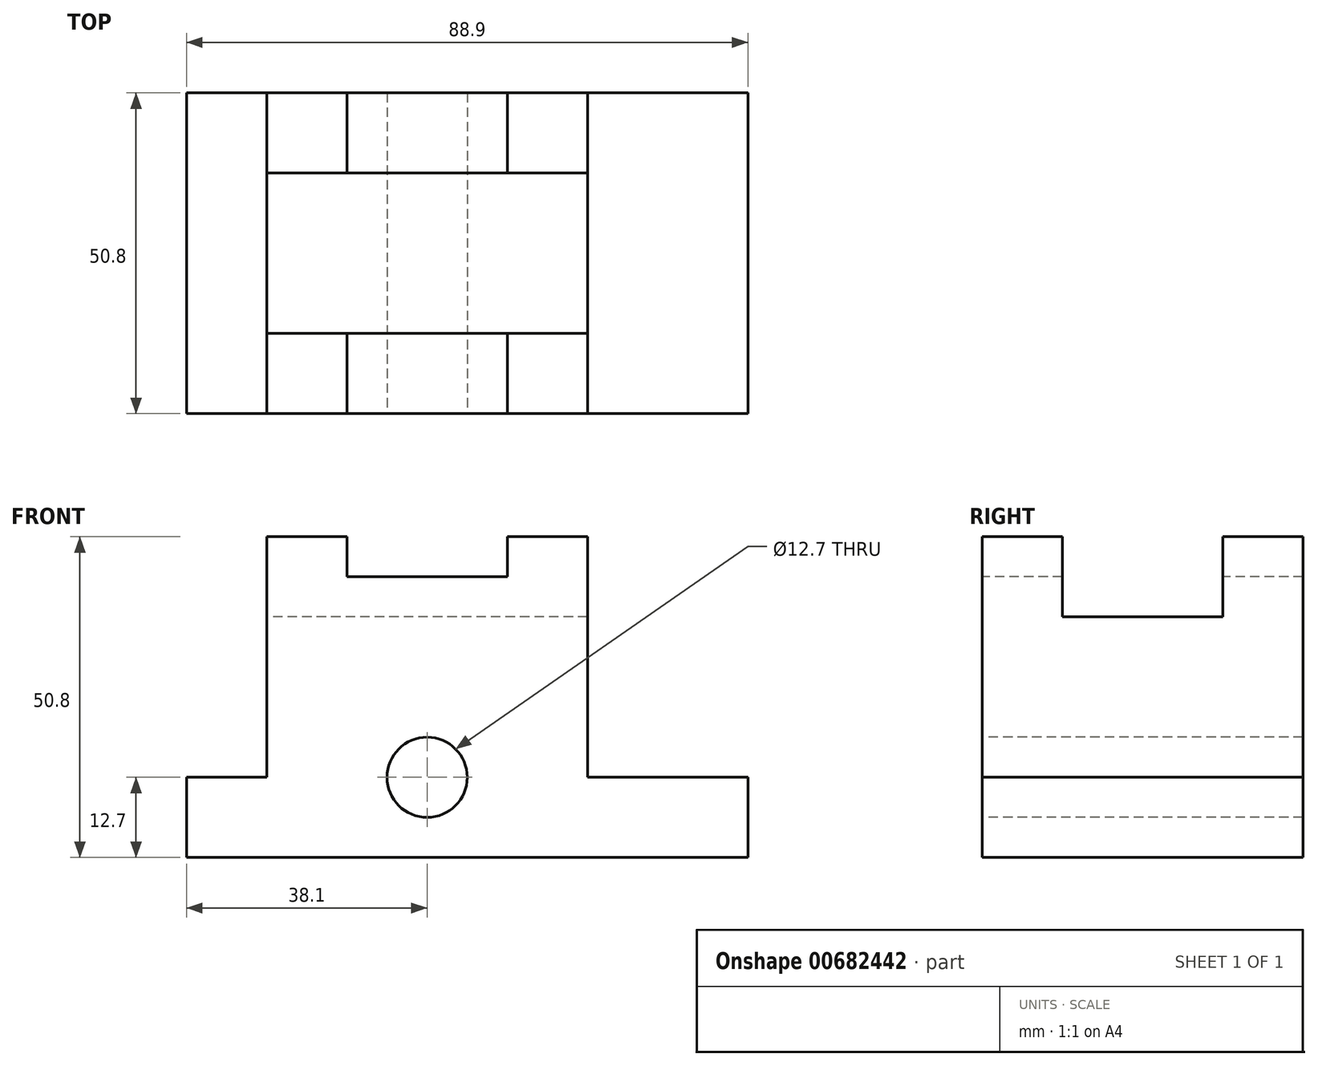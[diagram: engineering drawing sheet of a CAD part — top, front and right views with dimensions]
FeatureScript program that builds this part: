
annotation { "Feature Type Name" : "Feature", "Feature Type Description" : "" }
export const myFeature = defineFeature(function(context is Context, id is Id, definition is map)
    precondition{}
    {
        {
            var Q0;
            Q0=qCreatedBy(makeId("Front.planeOp"),FACE);
            var sketch = newSketch(context, id + "F0", { "sketchPlane" : qUnion([Q0])});
            skLineSegment(sketch, "E0.bottom", {"start": v(-44.45, 19.05) * mm, "end": v(44.45, 19.05) * mm});
            skLineSegment(sketch, "E0.top", {"start": v(-44.45, -19.05) * mm, "end": v(44.45, -19.05) * mm});
            skLineSegment(sketch, "E0.left", {"start": v(-44.45, 19.05) * mm, "end": v(-44.45, -19.05) * mm});
            skLineSegment(sketch, "E0.right", {"start": v(44.45, 19.05) * mm, "end": v(44.45, -19.05) * mm});
            skPoint(sketch, "E0.middle", {"position": v(0, 0) * mm});
            skSolve(sketch);
        }
        {
            var Q0;
            Q0=makeQuery(id+"F0.imprint","IMPRINT",FACE,{"disambiguationData":[TD([[makeQuery(id+"F0.imprint","IMPRINT",EDGE,{"derivedFrom":sQuery(id+"F0.wireOp",EDGE,"E0.bottom")}),-1.0]])]});
            extrude(context, id + "F1", {"entities" : qUnion([Q0]), "depth" : 50.8 * mm, "offsetDistance" : 25.4 * mm});
        }
        {
            var Q0;
            Q0=makeQuery(id+"F1.opExtrude","CAP_FACE",FACE,{"disambiguationData":[OSD([sQuery(id+"F0.wireOp",EDGE,"E0.bottom"),sQuery(id+"F0.wireOp",EDGE,"E0.top"),sQuery(id+"F0.wireOp",EDGE,"E0.left"),sQuery(id+"F0.wireOp",EDGE,"E0.right")])],"isStart":false});
            var sketch = newSketch(context, id + "F2", { "sketchPlane" : qUnion([Q0])});
            skLineSegment(sketch, "E1.bottom", {"start": v(-44.45, 19.05) * mm, "end": v(-31.75, 19.05) * mm});
            skLineSegment(sketch, "E1.top", {"start": v(-44.45, -6.35) * mm, "end": v(-31.75, -6.35) * mm});
            skLineSegment(sketch, "E1.left", {"start": v(-44.45, 19.05) * mm, "end": v(-44.45, -6.35) * mm});
            skLineSegment(sketch, "E1.right", {"start": v(-31.75, 19.05) * mm, "end": v(-31.75, -6.35) * mm});
            skSolve(sketch);
        }
        {
            var Q0;
            Q0=makeQuery(id+"F2.imprint","IMPRINT",FACE,{"disambiguationData":[TD([[makeQuery(id+"F2.imprint","IMPRINT",EDGE,{"derivedFrom":sQuery(id+"F2.wireOp",EDGE,"E1.bottom")}),-1.0]])]});
            extrude(context, id + "F3", {"entities" : qUnion([Q0]), "operationType" : NewBodyOperationType.REMOVE, "endBound" : BoundingType.THROUGH_ALL, "oppositeDirection" : true, "depth" : 25.4 * mm, "offsetDistance" : 25.4 * mm});
        }
        {
            var Q0;
            Q0=makeQuery(id+"F1.opExtrude","CAP_FACE",FACE,{"disambiguationData":[OSD([sQuery(id+"F0.wireOp",EDGE,"E0.bottom"),sQuery(id+"F0.wireOp",EDGE,"E0.top"),sQuery(id+"F0.wireOp",EDGE,"E0.left"),sQuery(id+"F0.wireOp",EDGE,"E0.right")])],"isStart":false});
            var sketch = newSketch(context, id + "F4", { "sketchPlane" : qUnion([Q0])});
            skLineSegment(sketch, "E2.bottom", {"start": v(44.45, 19.05) * mm, "end": v(19.05, 19.05) * mm});
            skLineSegment(sketch, "E2.top", {"start": v(44.45, -6.35) * mm, "end": v(19.05, -6.35) * mm});
            skLineSegment(sketch, "E2.left", {"start": v(44.45, 19.05) * mm, "end": v(44.45, -6.35) * mm});
            skLineSegment(sketch, "E2.right", {"start": v(19.05, 19.05) * mm, "end": v(19.05, -6.35) * mm});
            skSolve(sketch);
        }
        {
            var Q0;
            Q0=makeQuery(id+"F4.imprint","IMPRINT",FACE,{"disambiguationData":[TD([[makeQuery(id+"F4.imprint","IMPRINT",EDGE,{"derivedFrom":sQuery(id+"F4.wireOp",EDGE,"E2.bottom")}),-1.0]])]});
            extrude(context, id + "F5", {"entities" : qUnion([Q0]), "operationType" : NewBodyOperationType.REMOVE, "endBound" : BoundingType.THROUGH_ALL, "oppositeDirection" : true, "depth" : 25.4 * mm, "offsetDistance" : 25.4 * mm});
        }
        {
            var Q0;
            Q0=makeQuery(id+"F1.opExtrude","SWEPT_FACE",FACE,{"disambiguationData":[OSD([sQuery(id+"F0.wireOp",EDGE,"E0.bottom")])]});
            var sketch = newSketch(context, id + "F6", { "sketchPlane" : qUnion([Q0])});
            skLineSegment(sketch, "E3.bottom", {"start": v(-31.75, 0) * mm, "end": v(19.05, 0) * mm});
            skLineSegment(sketch, "E3.top", {"start": v(-31.75, -12.7) * mm, "end": v(19.05, -12.7) * mm});
            skLineSegment(sketch, "E3.left", {"start": v(-31.75, 0) * mm, "end": v(-31.75, -12.7) * mm});
            skLineSegment(sketch, "E3.right", {"start": v(19.05, 0) * mm, "end": v(19.05, -12.7) * mm});
            skLineSegment(sketch, "E4.bottom", {"start": v(19.05, -50.8) * mm, "end": v(-31.75, -50.8) * mm});
            skLineSegment(sketch, "E4.top", {"start": v(19.05, -38.1) * mm, "end": v(-31.75, -38.1) * mm});
            skLineSegment(sketch, "E4.left", {"start": v(19.05, -50.8) * mm, "end": v(19.05, -38.1) * mm});
            skLineSegment(sketch, "E4.right", {"start": v(-31.75, -50.8) * mm, "end": v(-31.75, -38.1) * mm});
            skSolve(sketch);
        }
        {
            var Q0;
            Q0=makeQuery(id+"F6.imprint","IMPRINT",FACE,{"disambiguationData":[TD([[makeQuery(id+"F6.imprint","IMPRINT",EDGE,{"derivedFrom":sQuery(id+"F6.wireOp",EDGE,"E3.bottom")}),-1.0]])]});
            var Q1;
            Q1=makeQuery(id+"F6.imprint","IMPRINT",FACE,{"disambiguationData":[TD([[makeQuery(id+"F6.imprint","IMPRINT",EDGE,{"derivedFrom":sQuery(id+"F6.wireOp",EDGE,"E4.bottom")}),1.0]])]});
            extrude(context, id + "F7", {"entities" : qUnion([Q0, Q1]), "operationType" : NewBodyOperationType.ADD, "depth" : 6.35 * mm, "offsetDistance" : 25.4 * mm});
        }
        {
            var Q0;
            Q0=makeQuery(id+"F7.opExtrude","CAP_FACE",FACE,{"disambiguationData":[OSD([sQuery(id+"F6.wireOp",EDGE,"E3.bottom"),sQuery(id+"F6.wireOp",EDGE,"E3.top"),sQuery(id+"F6.wireOp",EDGE,"E3.left"),sQuery(id+"F6.wireOp",EDGE,"E3.right")])],"isStart":false});
            var sketch = newSketch(context, id + "F8", { "sketchPlane" : qUnion([Q0])});
            skLineSegment(sketch, "E5.bottom", {"start": v(-31.75, 0) * mm, "end": v(-19.05, 0) * mm});
            skLineSegment(sketch, "E5.top", {"start": v(-31.75, -12.7) * mm, "end": v(-19.05, -12.7) * mm});
            skLineSegment(sketch, "E5.left", {"start": v(-31.75, 0) * mm, "end": v(-31.75, -12.7) * mm});
            skLineSegment(sketch, "E5.right", {"start": v(-19.05, 0) * mm, "end": v(-19.05, -12.7) * mm});
            skLineSegment(sketch, "E6.bottom", {"start": v(19.05, 0) * mm, "end": v(6.35, 0) * mm});
            skLineSegment(sketch, "E6.top", {"start": v(19.05, -12.7) * mm, "end": v(6.35, -12.7) * mm});
            skLineSegment(sketch, "E6.left", {"start": v(19.05, 0) * mm, "end": v(19.05, -12.7) * mm});
            skLineSegment(sketch, "E6.right", {"start": v(6.35, 0) * mm, "end": v(6.35, -12.7) * mm});
            skSolve(sketch);
        }
        {
            var Q0;
            Q0=makeQuery(id+"F8.imprint","IMPRINT",FACE,{"disambiguationData":[TD([[makeQuery(id+"F8.imprint","IMPRINT",EDGE,{"derivedFrom":sQuery(id+"F8.wireOp",EDGE,"E5.bottom")}),-1.0]])]});
            var Q1;
            Q1=makeQuery(id+"F8.imprint","IMPRINT",FACE,{"disambiguationData":[TD([[makeQuery(id+"F8.imprint","IMPRINT",EDGE,{"derivedFrom":sQuery(id+"F8.wireOp",EDGE,"E6.bottom")}),-1.0]])]});
            extrude(context, id + "F9", {"entities" : qUnion([Q0, Q1]), "operationType" : NewBodyOperationType.ADD, "depth" : 6.35 * mm, "offsetDistance" : 25.4 * mm});
        }
        {
            var Q0;
            Q0=makeQuery(id+"F7.opExtrude","CAP_FACE",FACE,{"disambiguationData":[OSD([sQuery(id+"F6.wireOp",EDGE,"E4.bottom"),sQuery(id+"F6.wireOp",EDGE,"E4.top"),sQuery(id+"F6.wireOp",EDGE,"E4.left"),sQuery(id+"F6.wireOp",EDGE,"E4.right")])],"isStart":false});
            var sketch = newSketch(context, id + "F10", { "sketchPlane" : qUnion([Q0])});
            skLineSegment(sketch, "E7.bottom", {"start": v(-31.75, -38.1) * mm, "end": v(-19.05, -38.1) * mm});
            skLineSegment(sketch, "E7.top", {"start": v(-31.75, -50.8) * mm, "end": v(-19.05, -50.8) * mm});
            skLineSegment(sketch, "E7.left", {"start": v(-31.75, -38.1) * mm, "end": v(-31.75, -50.8) * mm});
            skLineSegment(sketch, "E7.right", {"start": v(-19.05, -38.1) * mm, "end": v(-19.05, -50.8) * mm});
            skLineSegment(sketch, "E8.bottom", {"start": v(19.05, -38.1) * mm, "end": v(6.35, -38.1) * mm});
            skLineSegment(sketch, "E8.top", {"start": v(19.05, -50.8) * mm, "end": v(6.35, -50.8) * mm});
            skLineSegment(sketch, "E8.left", {"start": v(19.05, -38.1) * mm, "end": v(19.05, -50.8) * mm});
            skLineSegment(sketch, "E8.right", {"start": v(6.35, -38.1) * mm, "end": v(6.35, -50.8) * mm});
            skSolve(sketch);
        }
        {
            var Q0;
            Q0=makeQuery(id+"F10.imprint","IMPRINT",FACE,{"disambiguationData":[TD([[makeQuery(id+"F10.imprint","IMPRINT",EDGE,{"derivedFrom":sQuery(id+"F10.wireOp",EDGE,"E7.bottom")}),1.0]])]});
            var Q1;
            Q1=makeQuery(id+"F10.imprint","IMPRINT",FACE,{"disambiguationData":[TD([[makeQuery(id+"F10.imprint","IMPRINT",EDGE,{"derivedFrom":sQuery(id+"F10.wireOp",EDGE,"E8.bottom")}),1.0]])]});
            extrude(context, id + "F11", {"entities" : qUnion([Q0, Q1]), "operationType" : NewBodyOperationType.ADD, "depth" : 6.35 * mm, "offsetDistance" : 25.4 * mm});
        }
        {
            var Q0;
            Q0=makeQuery(id+"F11.boolean.opBoolean","MERGE",FACE,{"derivedFrom":[makeQuery(id+"F7.boolean.opBoolean","MERGE",FACE,{"derivedFrom":[makeQuery(id+"F1.opExtrude","CAP_FACE",FACE,{"disambiguationData":[OSD([sQuery(id+"F0.wireOp",EDGE,"E0.bottom"),sQuery(id+"F0.wireOp",EDGE,"E0.top"),sQuery(id+"F0.wireOp",EDGE,"E0.left"),sQuery(id+"F0.wireOp",EDGE,"E0.right")])],"isStart":false}),makeQuery(id+"F7.opExtrude","SWEPT_FACE",FACE,{"disambiguationData":[OSD([sQuery(id+"F6.wireOp",EDGE,"E4.bottom")])]})]}),makeQuery(id+"F11.opExtrude","SWEPT_FACE",FACE,{"disambiguationData":[OSD([sQuery(id+"F10.wireOp",EDGE,"E7.top")])]}),makeQuery(id+"F11.opExtrude","SWEPT_FACE",FACE,{"disambiguationData":[OSD([sQuery(id+"F10.wireOp",EDGE,"E8.top")])]})]});
            var sketch = newSketch(context, id + "F12", { "sketchPlane" : qUnion([Q0])});
            skCircle(sketch, "E9", {"center": v(-6.35, -6.35) * mm, "radius": 6.35 * mm});
            skSolve(sketch);
        }
        {
            var Q0;
            Q0=makeQuery(id+"F12.imprint","IMPRINT",FACE,{"disambiguationData":[TD([[makeQuery(id+"F12.imprint","IMPRINT",EDGE,{"derivedFrom":sQuery(id+"F12.wireOp",EDGE,"E9")}),1.0]])]});
            extrude(context, id + "F13", {"entities" : qUnion([Q0]), "operationType" : NewBodyOperationType.REMOVE, "endBound" : BoundingType.THROUGH_ALL, "oppositeDirection" : true, "depth" : 25.4 * mm, "offsetDistance" : 25.4 * mm});
        }
    });
